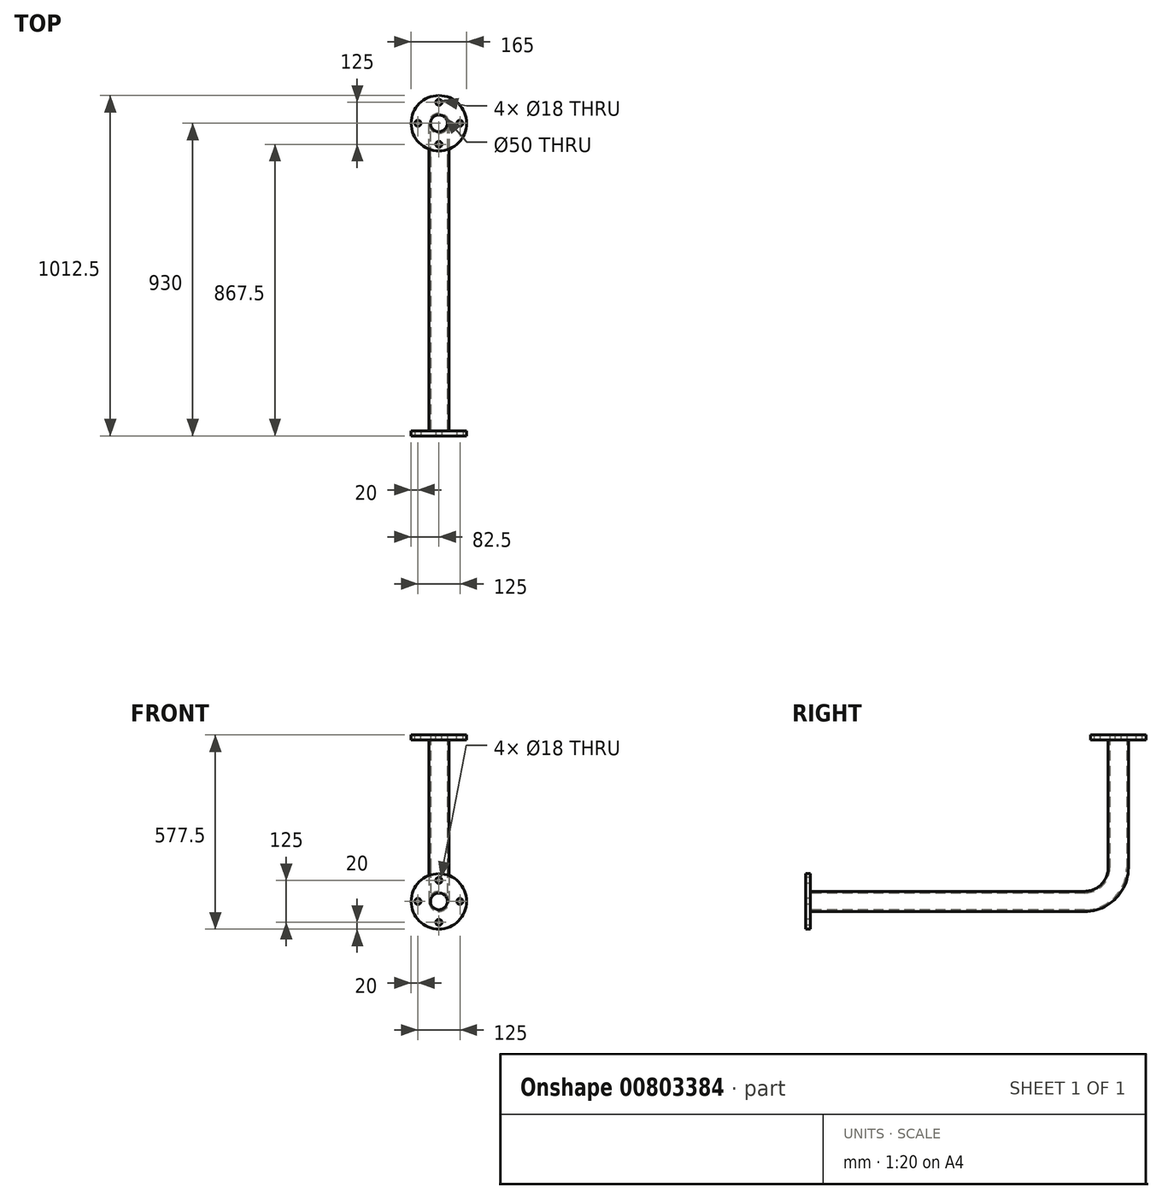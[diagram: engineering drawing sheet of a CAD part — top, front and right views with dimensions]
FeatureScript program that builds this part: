
annotation { "Feature Type Name" : "Feature", "Feature Type Description" : "" }
export const myFeature = defineFeature(function(context is Context, id is Id, definition is map)
    precondition{}
    {
        {
            var Q0;
            Q0=qCreatedBy(makeId("Right.planeOp"),FACE);
            var sketch = newSketch(context, id + "F0", { "sketchPlane" : qUnion([Q0])});
            skLineSegment(sketch, "E0", {"start": v(0, 0) * mm, "end": v(0, -395) * mm});
            skLineSegment(sketch, "E1", {"start": v(-100, -495) * mm, "end": v(-930, -495) * mm});
            skPoint(sketch, "E2.visualSharp", {"position": v(0, -495) * mm});
            skArc(sketch, "E2.filletArc", {"start": v(-100, -495) * mm, "mid": v(-29.29, -465.71) * mm, "end": v(0, -395) * mm});
            skSolve(sketch);
        }
        {
            var Q0;
            Q0=qCreatedBy(makeId("Top.planeOp"),FACE);
            var sketch = newSketch(context, id + "F1", { "sketchPlane" : qUnion([Q0])});
            skCircle(sketch, "E3", {"center": v(0, 0) * mm, "radius": 25 * mm});
            skCircle(sketch, "E4", {"center": v(0, 0) * mm, "radius": 30 * mm});
            skSolve(sketch);
        }
        {
            var Q0;
            Q0=makeQuery(id+"F1.imprint","IMPRINT",FACE,{"disambiguationData":[TD([[makeQuery(id+"F1.imprint","IMPRINT",EDGE,{"derivedFrom":sQuery(id+"F1.wireOp",EDGE,"E3")}),-1.0]])]});
            var Q1;
            Q1=sQuery(id+"F0.wireOp",EDGE,"E0");
            var Q2;
            Q2=sQuery(id+"F0.wireOp",EDGE,"E2.filletArc");
            var Q3;
            Q3=sQuery(id+"F0.wireOp",EDGE,"E1");
            sweep(context, id + "F2", {"profiles" : qUnion([Q0]), "path" : qUnion([Q1, Q2, Q3])});
        }
        {
            var Q0;
            Q0=qCreatedBy(makeId("Top.planeOp"),FACE);
            var sketch = newSketch(context, id + "F3", { "sketchPlane" : qUnion([Q0])});
            skCircle(sketch, "E5", {"center": v(0, 0) * mm, "radius": 82.5 * mm});
            skCircle(sketch, "E6", {"center": v(0, -62.5) * mm, "radius": 9 * mm});
            skCircle(sketch, "E7.0", {"center": v(0, 0) * mm, "radius": 25 * mm});
            skCircle(sketch, "E8.1.0", {"center": v(62.5, 0) * mm, "radius": 9 * mm});
            skCircle(sketch, "E8.2.0", {"center": v(0, 62.5) * mm, "radius": 9 * mm});
            skCircle(sketch, "E8.3.0", {"center": v(-62.5, 0) * mm, "radius": 9 * mm});
            skSolve(sketch);
        }
        {
            var Q0;
            Q0=makeQuery(id+"F3.imprint","IMPRINT",FACE,{"disambiguationData":[TD([[makeQuery(id+"F3.imprint","IMPRINT",EDGE,{"derivedFrom":sQuery(id+"F3.wireOp",EDGE,"E5")}),1.0]])]});
            extrude(context, id + "F4", {"entities" : qUnion([Q0]), "operationType" : NewBodyOperationType.ADD, "oppositeDirection" : true, "depth" : 15 * mm, "offsetDistance" : 25 * mm});
        }
        {
            var Q0;
            Q0=makeQuery(id+"F2.opSweep","CAP_FACE",FACE,{"disambiguationData":[OSD([sQuery(id+"F0.wireOp",VERTEX,"E1.end"),sQuery(id+"F1.wireOp",EDGE,"E3"),sQuery(id+"F1.wireOp",EDGE,"E4")])],"isStart":false});
            var sketch = newSketch(context, id + "F5", { "sketchPlane" : qUnion([Q0])});
            skCircle(sketch, "E9", {"center": v(0, -495) * mm, "radius": 82.5 * mm});
            skCircle(sketch, "E10", {"center": v(0, -432.5) * mm, "radius": 9 * mm});
            skCircle(sketch, "E11.1.0", {"center": v(-62.5, -495) * mm, "radius": 9 * mm});
            skCircle(sketch, "E11.2.0", {"center": v(0, -557.5) * mm, "radius": 9 * mm});
            skCircle(sketch, "E11.3.0", {"center": v(62.5, -495) * mm, "radius": 9 * mm});
            skCircle(sketch, "E12.0", {"center": v(0, -495) * mm, "radius": 25 * mm});
            skSolve(sketch);
        }
        {
            var Q0;
            Q0=makeQuery(id+"F5.imprint","IMPRINT",FACE,{"disambiguationData":[TD([[makeQuery(id+"F5.imprint","IMPRINT",EDGE,{"derivedFrom":sQuery(id+"F5.wireOp",EDGE,"E9")}),1.0]])]});
            extrude(context, id + "F6", {"entities" : qUnion([Q0]), "operationType" : NewBodyOperationType.ADD, "oppositeDirection" : true, "depth" : 15 * mm, "offsetDistance" : 25 * mm});
        }
    });
